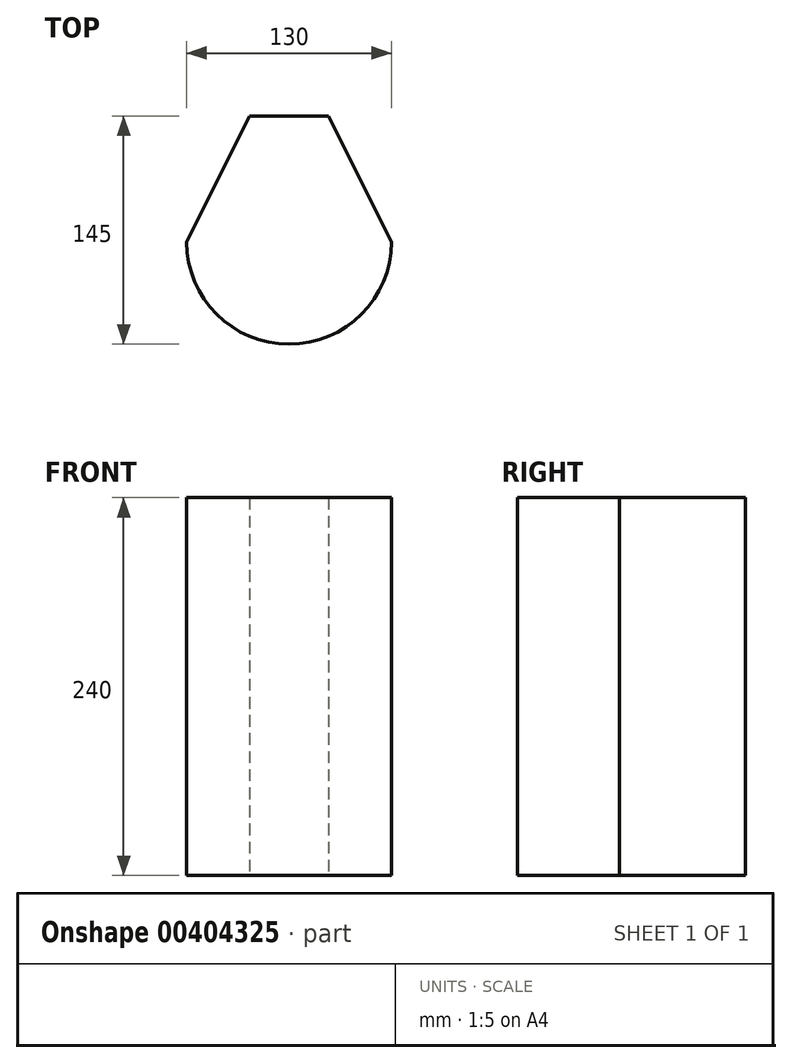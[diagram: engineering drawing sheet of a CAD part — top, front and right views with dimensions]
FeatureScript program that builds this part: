
annotation { "Feature Type Name" : "Feature", "Feature Type Description" : "" }
export const myFeature = defineFeature(function(context is Context, id is Id, definition is map)
    precondition{}
    {
        {
            var Q0;
            Q0=qCreatedBy(makeId("Top.planeOp"),FACE);
            var sketch = newSketch(context, id + "F0", { "sketchPlane" : qUnion([Q0])});
            skArc(sketch, "E0", {"start": v(-65, 0) * mm, "mid": v(0, -65) * mm, "end": v(65, 0) * mm});
            skLineSegment(sketch, "E1", {"start": v(-25, 80) * mm, "end": v(25, 80) * mm});
            skLineSegment(sketch, "E2", {"start": v(-65, 0) * mm, "end": v(-25, 80) * mm});
            skLineSegment(sketch, "E3", {"start": v(65, 0) * mm, "end": v(25, 80) * mm});
            skSolve(sketch);
        }
        {
            var Q0;
            Q0 = qSketchRegion(id + "F0", true);
            extrude(context, id + "F1", {"entities" : qUnion([Q0]), "depth" : 240 * mm});
        }
    });
